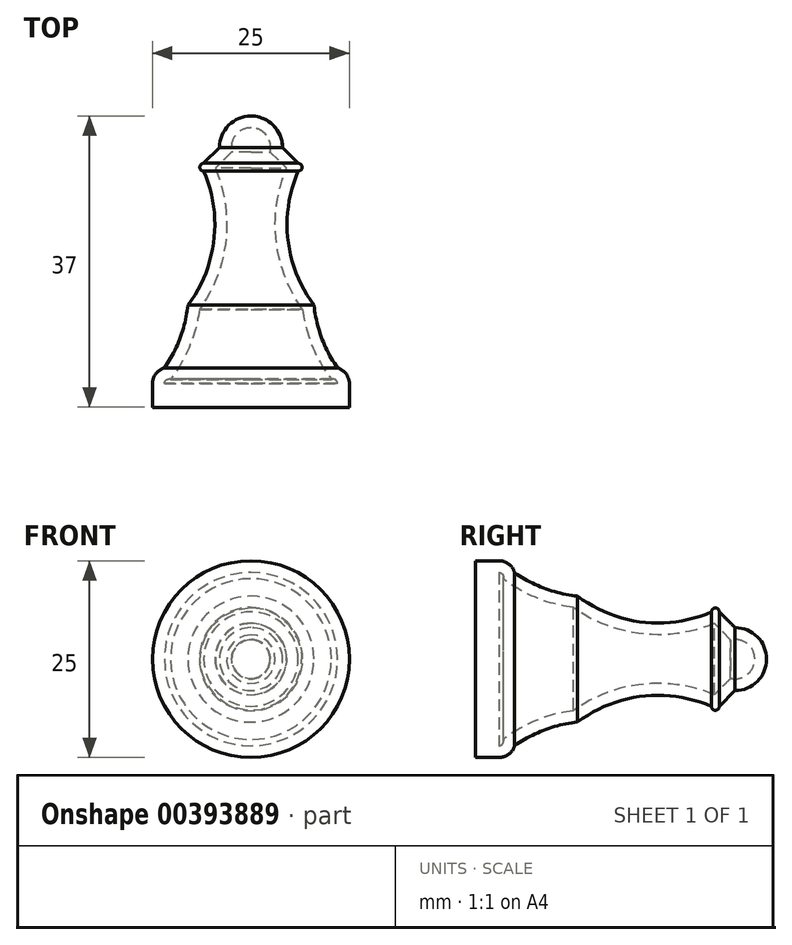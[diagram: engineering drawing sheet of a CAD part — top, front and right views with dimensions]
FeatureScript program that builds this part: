
annotation { "Feature Type Name" : "Feature", "Feature Type Description" : "" }
export const myFeature = defineFeature(function(context is Context, id is Id, definition is map)
    precondition{}
    {
        {
            var Q0;
            Q0=qCreatedBy(makeId("Top.planeOp"),FACE);
            var sketch = newSketch(context, id + "F0", { "sketchPlane" : qUnion([Q0])});
            skLineSegment(sketch, "E0", {"start": v(0, 22.6) * mm, "end": v(0, 16.13) * mm, "construction": true});
            skLineSegment(sketch, "E1", {"start": v(0, -20.87) * mm, "end": v(-12.5, -20.87) * mm});
            skArc(sketch, "E2", {"start": v(-11, -15.87) * mm, "mid": v(-8.99, -12.07) * mm, "end": v(-8, -7.87) * mm});
            skLineSegment(sketch, "E3", {"start": v(-12.5, -20.87) * mm, "end": v(-12.5, -17.87) * mm});
            skArc(sketch, "E4", {"start": v(-11, -15.87) * mm, "mid": v(-12.08, -16.62) * mm, "end": v(-12.5, -17.87) * mm});
            skArc(sketch, "E5", {"start": v(-8, -7.87) * mm, "mid": v(-4.7, 0.36) * mm, "end": v(-6, 9.13) * mm});
            skArc(sketch, "E6", {"start": v(-6, 10.13) * mm, "mid": v(-6.5, 9.63) * mm, "end": v(-6, 9.13) * mm});
            skLineSegment(sketch, "E7", {"start": v(-4, 12.13) * mm, "end": v(-6, 10.13) * mm});
            skArc(sketch, "E8", {"start": v(0, 16.13) * mm, "mid": v(-2.83, 14.95) * mm, "end": v(-4, 12.13) * mm});
            skLineSegment(sketch, "E9.trimOffspring", {"start": v(0, -20.87) * mm, "end": v(0, -25.95) * mm, "construction": true});
            skLineSegment(sketch, "E10", {"start": v(0, 16.13) * mm, "end": v(0, -20.87) * mm});
            skSolve(sketch);
        }
        {
            var Q0;
            Q0 = qSketchRegion(id + "F0", true);
            var Q1;
            Q1=sQuery(id+"F0.wireOp",EDGE,"E0");
            revolve(context, id + "F1", {"entities" : qUnion([Q0]), "axis" : qUnion([Q1]), "revolveType" : RevolveType.FULL});
        }
        {
            var Q0;
            Q0=makeQuery(id+"F1.opRevolve","SWEPT_FACE",FACE,{"disambiguationData":[OSD([sQuery(id+"F0.wireOp",EDGE,"E1")])]});
            shell(context, id + "F2", {"entities" : qUnion([Q0]), "thickness" : 1.5 * mm});
        }
        {
            var Q0;
            Q0=makeQuery(id+"F1.opRevolve","SWEPT_FACE",FACE,{"disambiguationData":[OSD([sQuery(id+"F0.wireOp",EDGE,"E1")])]});
            var sketch = newSketch(context, id + "F3", { "sketchPlane" : qUnion([Q0])});
            skCircle(sketch, "E11", {"center": v(0, 0) * mm, "radius": 12.5 * mm});
            skSolve(sketch);
        }
        {
            var Q0;
            Q0 = qSketchRegion(id + "F3", true);
            extrude(context, id + "F4", {"entities" : qUnion([Q0]), "operationType" : NewBodyOperationType.ADD, "oppositeDirection" : true, "depth" : 3 * mm});
        }
    });
